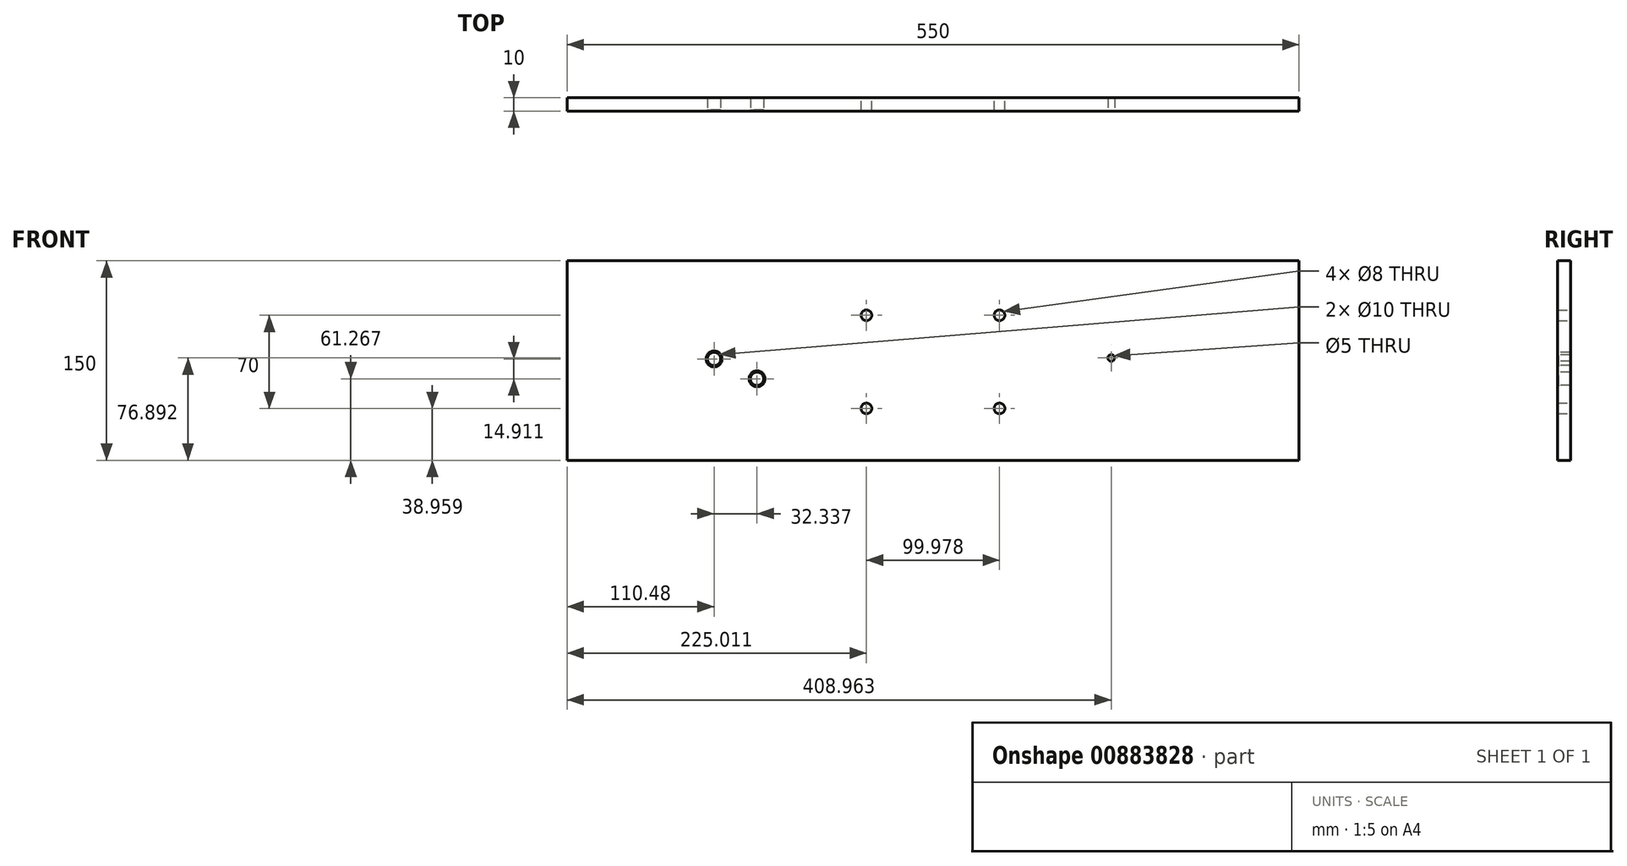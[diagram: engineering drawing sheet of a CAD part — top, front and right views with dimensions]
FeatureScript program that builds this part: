
annotation { "Feature Type Name" : "Feature", "Feature Type Description" : "" }
export const myFeature = defineFeature(function(context is Context, id is Id, definition is map)
    precondition{}
    {
        {
            var Q0;
            Q0=qCreatedBy(makeId("Front.planeOp"),FACE);
            var sketch = newSketch(context, id + "F0", { "sketchPlane" : qUnion([Q0])});
            skLineSegment(sketch, "E0", {"start": v(-275, 0) * mm, "end": v(275, 0) * mm});
            skLineSegment(sketch, "E1", {"start": v(275, 0) * mm, "end": v(275, -150) * mm});
            skLineSegment(sketch, "E2", {"start": v(275, -150) * mm, "end": v(-275, -150) * mm});
            skLineSegment(sketch, "E3", {"start": v(-275, -150) * mm, "end": v(-275, 0) * mm});
            skLineSegment(sketch, "E4", {"start": v(0, 0) * mm, "end": v(50, 0) * mm});
            skCircle(sketch, "E5.1.0.0", {"center": v(49.99, -111.04) * mm, "radius": 4 * mm});
            skCircle(sketch, "E5.1.0.1", {"center": v(49.99, -41.04) * mm, "radius": 4 * mm});
            skCircle(sketch, "E6.MirrorC", {"center": v(-49.99, -111.04) * mm, "radius": 4 * mm});
            skCircle(sketch, "E7.MirrorC", {"center": v(-49.99, -41.04) * mm, "radius": 4 * mm});
            skSolve(sketch);
        }
        {
            var Q0;
            Q0=makeQuery(id+"F0.imprint","IMPRINT",FACE,{"disambiguationData":[TD([[makeQuery(id+"F0.imprint","IMPRINT",EDGE,{"derivedFrom":sQuery(id+"F0.wireOp",EDGE,"E0")}),-1.0]])]});
            extrude(context, id + "F1", {"entities" : qUnion([Q0]), "depth" : 10 * mm, "offsetDistance" : 25 * mm});
        }
        {
            var Q0;
            Q0=makeQuery(id+"F1.opExtrude","CAP_FACE",FACE,{"disambiguationData":[OSD([sQuery(id+"F0.wireOp",EDGE,"E0"),sQuery(id+"F0.wireOp",EDGE,"E1"),sQuery(id+"F0.wireOp",EDGE,"E2"),sQuery(id+"F0.wireOp",EDGE,"E3"),sQuery(id+"F0.wireOp",EDGE,"E4"),sQuery(id+"F0.wireOp",EDGE,"E5.1.0.0"),sQuery(id+"F0.wireOp",EDGE,"E5.1.0.1"),sQuery(id+"F0.wireOp",EDGE,"E6.MirrorC"),sQuery(id+"F0.wireOp",EDGE,"E7.MirrorC")])],"isStart":false});
            var sketch = newSketch(context, id + "F2", { "sketchPlane" : qUnion([Q0])});
            skPoint(sketch, "E8", {"position": v(-164.52, -73.82) * mm});
            skPoint(sketch, "E9", {"position": v(-132.18, -88.73) * mm});
            skSolve(sketch);
        }
        {
            var Q0;
            Q0=sQuery(id+"F2.wireOp",VERTEX,"E9");
            var Q1;
            Q1=makeQuery(id+"F1.opExtrude","SWEPT_BODY",BODY,{"disambiguationData":[OSD([sQuery(id+"F0.wireOp",EDGE,"E0"),sQuery(id+"F0.wireOp",EDGE,"E1"),sQuery(id+"F0.wireOp",EDGE,"E2"),sQuery(id+"F0.wireOp",EDGE,"E3"),sQuery(id+"F0.wireOp",EDGE,"E4"),sQuery(id+"F0.wireOp",EDGE,"E5.1.0.0"),sQuery(id+"F0.wireOp",EDGE,"E5.1.0.1"),sQuery(id+"F0.wireOp",EDGE,"E6.MirrorC"),sQuery(id+"F0.wireOp",EDGE,"E7.MirrorC")])]});
            hole(context, id + "F3", {"style" : HoleStyle.C_SINK, "endStyle" : HoleEndStyle.THROUGH, "holeDiameter" : 10 * mm, "cSinkDiameter" : 12 * mm, "cSinkAngle" : 90 * degree, "majorDiameter" : 5 * mm, "isTappedThrough" : true, "tappedDepth" : 12 * mm, "tapClearance" : 3, "startFromSketch" : true, "locations" : qUnion([Q0]), "scope" : qUnion([Q1])});
        }
        {
            var Q0;
            Q0=sQuery(id+"F2.wireOp",VERTEX,"E8");
            var Q1;
            Q1=makeQuery(id+"F1.opExtrude","SWEPT_BODY",BODY,{"disambiguationData":[OSD([sQuery(id+"F0.wireOp",EDGE,"E0"),sQuery(id+"F0.wireOp",EDGE,"E1"),sQuery(id+"F0.wireOp",EDGE,"E2"),sQuery(id+"F0.wireOp",EDGE,"E3"),sQuery(id+"F0.wireOp",EDGE,"E4"),sQuery(id+"F0.wireOp",EDGE,"E5.1.0.0"),sQuery(id+"F0.wireOp",EDGE,"E5.1.0.1"),sQuery(id+"F0.wireOp",EDGE,"E6.MirrorC"),sQuery(id+"F0.wireOp",EDGE,"E7.MirrorC")])]});
            hole(context, id + "F4", {"style" : HoleStyle.C_SINK, "endStyle" : HoleEndStyle.THROUGH, "holeDiameter" : 10 * mm, "cSinkDiameter" : 12 * mm, "cSinkAngle" : 90 * degree, "majorDiameter" : 5 * mm, "isTappedThrough" : true, "tappedDepth" : 12 * mm, "tapClearance" : 3, "startFromSketch" : true, "locations" : qUnion([Q0]), "scope" : qUnion([Q1])});
        }
        {
            var Q0;
            Q0=makeQuery(id+"F2.imprint","IMPRINT",FACE,{"disambiguationData":[TD([[makeQuery(id+"F2.imprint","IMPRINT",EDGE,{"derivedFrom":makeQuery(id+"F1.opExtrude","CAP_EDGE",EDGE,{"disambiguationData":[OSD([sQuery(id+"F0.wireOp",EDGE,"E1")])],"isStart":false})}),-1.0]])]});
            var sketch = newSketch(context, id + "F5", { "sketchPlane" : qUnion([Q0])});
            skPoint(sketch, "E10", {"position": v(133.96, -73.1) * mm});
            skSolve(sketch);
        }
        {
            var Q0;
            Q0=sQuery(id+"F5.wireOp",VERTEX,"E10");
            var Q1;
            Q1=makeQuery(id+"F1.opExtrude","SWEPT_BODY",BODY,{"disambiguationData":[OSD([sQuery(id+"F0.wireOp",EDGE,"E0"),sQuery(id+"F0.wireOp",EDGE,"E1"),sQuery(id+"F0.wireOp",EDGE,"E2"),sQuery(id+"F0.wireOp",EDGE,"E3"),sQuery(id+"F0.wireOp",EDGE,"E4"),sQuery(id+"F0.wireOp",EDGE,"E5.1.0.0"),sQuery(id+"F0.wireOp",EDGE,"E5.1.0.1"),sQuery(id+"F0.wireOp",EDGE,"E6.MirrorC"),sQuery(id+"F0.wireOp",EDGE,"E7.MirrorC")])]});
            hole(context, id + "F6", {"style" : HoleStyle.SIMPLE, "endStyle" : HoleEndStyle.THROUGH, "holeDiameter" : 5 * mm, "majorDiameter" : 5 * mm, "isTappedThrough" : true, "tappedDepth" : 12 * mm, "tapClearance" : 3, "locations" : qUnion([Q0]), "scope" : qUnion([Q1])});
        }
    });
